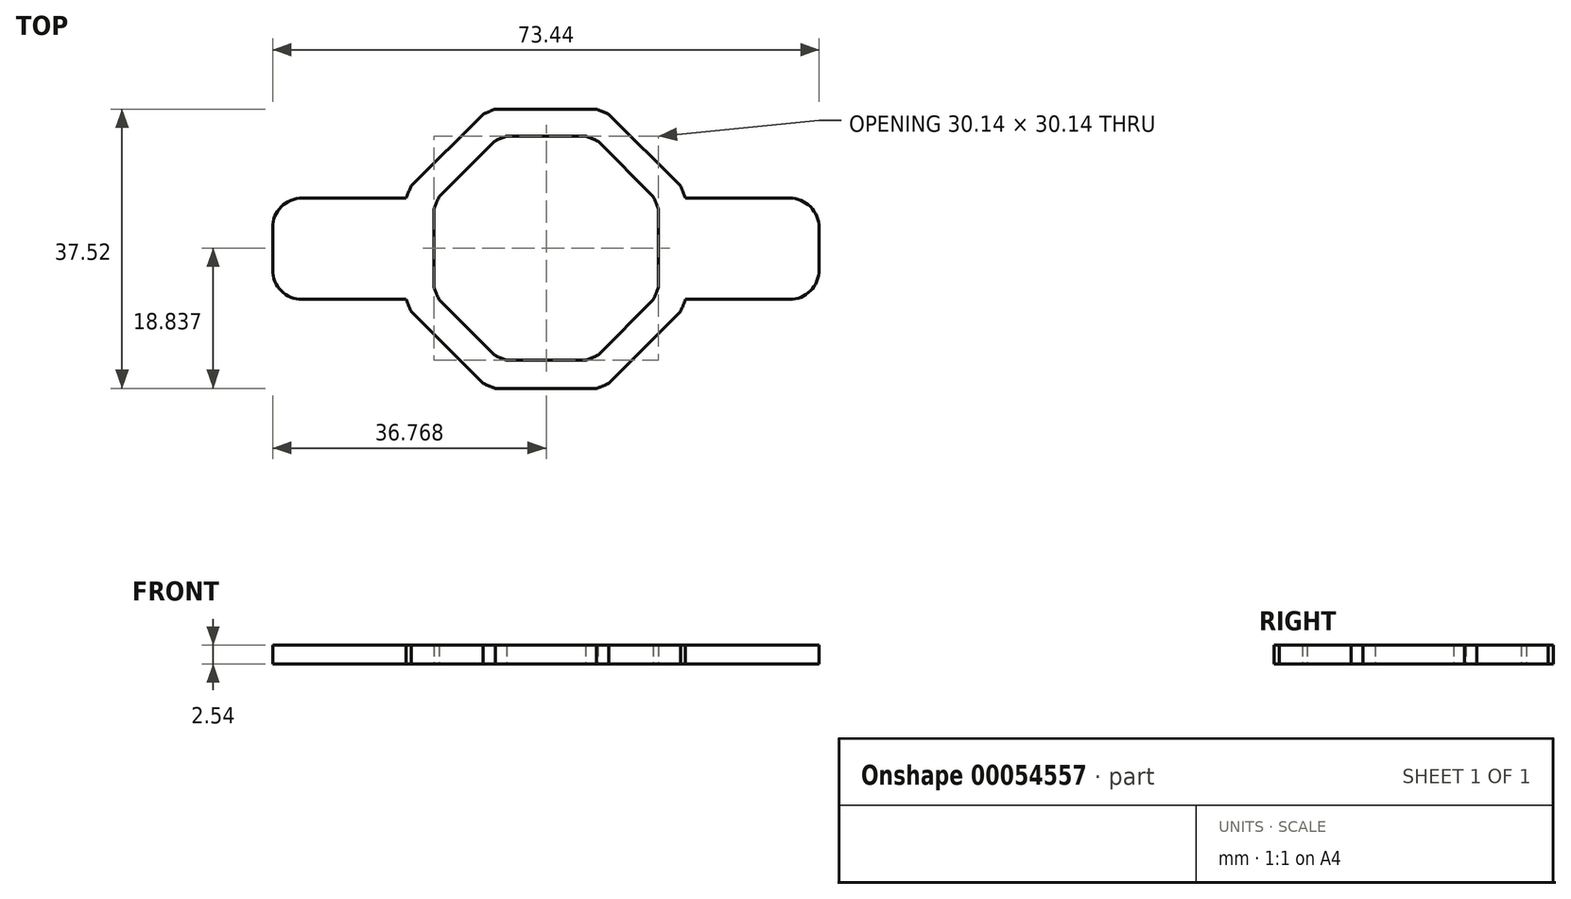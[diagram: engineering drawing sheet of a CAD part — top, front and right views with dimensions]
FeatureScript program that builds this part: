
annotation { "Feature Type Name" : "Feature", "Feature Type Description" : "" }
export const myFeature = defineFeature(function(context is Context, id is Id, definition is map)
    precondition{}
    {
        {
            var Q0;
            Q0=qCreatedBy(makeId("Top.planeOp"),FACE);
            var sketch = newSketch(context, id + "F0", { "sketchPlane" : qUnion([Q0])});
            skArc(sketch, "E0", {"start": v(-18.08, 8.45) * mm, "mid": v(-18.44, 7.64) * mm, "end": v(-18.76, 6.8) * mm});
            skLineSegment(sketch, "E1", {"start": v(-6.8, 18.76) * mm, "end": v(6.8, 18.76) * mm});
            skPoint(sketch, "E2.end.orphan", {"position": v(0, 18.76) * mm});
            skPoint(sketch, "E2.start.orphan", {"position": v(0, 19.96) * mm});
            skLineSegment(sketch, "E3.1.0", {"start": v(-18.08, 8.45) * mm, "end": v(-8.45, 18.08) * mm});
            skLineSegment(sketch, "E3.2.0", {"start": v(-18.76, -6.8) * mm, "end": v(-18.76, 6.8) * mm});
            skLineSegment(sketch, "E3.3.0", {"start": v(-8.45, -18.08) * mm, "end": v(-18.08, -8.45) * mm});
            skLineSegment(sketch, "E3.4.0", {"start": v(6.8, -18.76) * mm, "end": v(-6.8, -18.76) * mm});
            skLineSegment(sketch, "E3.5.0", {"start": v(18.08, -8.45) * mm, "end": v(8.45, -18.08) * mm});
            skLineSegment(sketch, "E3.6.0", {"start": v(18.76, 6.8) * mm, "end": v(18.76, -6.8) * mm});
            skLineSegment(sketch, "E3.7.0", {"start": v(8.45, 18.08) * mm, "end": v(18.08, 8.45) * mm});
            skArc(sketch, "E4.trimOffspring", {"start": v(-6.8, 18.76) * mm, "mid": v(-7.64, 18.44) * mm, "end": v(-8.45, 18.08) * mm});
            skArc(sketch, "E5.trimOffspring", {"start": v(8.45, 18.08) * mm, "mid": v(7.64, 18.44) * mm, "end": v(6.8, 18.76) * mm});
            skArc(sketch, "E6.trimOffspring", {"start": v(18.76, 6.8) * mm, "mid": v(18.44, 7.64) * mm, "end": v(18.08, 8.45) * mm});
            skArc(sketch, "E7.trimOffspring", {"start": v(18.08, -8.45) * mm, "mid": v(18.44, -7.64) * mm, "end": v(18.76, -6.8) * mm});
            skArc(sketch, "E8.trimOffspring", {"start": v(-8.45, -18.08) * mm, "mid": v(-7.64, -18.44) * mm, "end": v(-6.8, -18.76) * mm});
            skArc(sketch, "E9.trimOffspring", {"start": v(-18.76, -6.8) * mm, "mid": v(-18.44, -7.64) * mm, "end": v(-18.08, -8.45) * mm});
            skArc(sketch, "E10.trimOffspring", {"start": v(6.8, -18.76) * mm, "mid": v(7.64, -18.44) * mm, "end": v(8.45, -18.08) * mm});
            skLineSegment(sketch, "E11.6.0", {"start": v(15.12, 5.36) * mm, "end": v(15.12, -5.2) * mm});
            skLineSegment(sketch, "E11.4.0", {"start": v(5.33, -15) * mm, "end": v(-5.23, -15) * mm});
            skLineSegment(sketch, "E11.3.0", {"start": v(-6.87, -14.31) * mm, "end": v(-14.34, -6.84) * mm});
            skLineSegment(sketch, "E11.7.0", {"start": v(6.97, 14.46) * mm, "end": v(14.43, 7) * mm});
            skLineSegment(sketch, "E11.5.0", {"start": v(14.43, -6.84) * mm, "end": v(6.97, -14.31) * mm});
            skPoint(sketch, "E12.start.orphan", {"position": v(0.05, 16.04) * mm});
            skLineSegment(sketch, "E11.2.0", {"start": v(-15.02, -5.2) * mm, "end": v(-15.02, 5.36) * mm});
            skLineSegment(sketch, "E11.1.0", {"start": v(-14.34, 7) * mm, "end": v(-6.87, 14.46) * mm});
            skLineSegment(sketch, "E13", {"start": v(-5.23, 15.14) * mm, "end": v(5.33, 15.14) * mm});
            skPoint(sketch, "E12.end.orphan", {"position": v(0.05, 15.14) * mm});
            skPoint(sketch, "E11.center", {"position": v(0.05, 0.08) * mm});
            skArc(sketch, "E14.trimOffspring", {"start": v(5.33, -15) * mm, "mid": v(6.16, -14.67) * mm, "end": v(6.97, -14.31) * mm});
            skArc(sketch, "E15.trimOffspring", {"start": v(6.97, 14.46) * mm, "mid": v(6.16, 14.83) * mm, "end": v(5.33, 15.14) * mm});
            skArc(sketch, "E16.trimOffspring", {"start": v(-5.23, 15.14) * mm, "mid": v(-6.06, 14.83) * mm, "end": v(-6.87, 14.46) * mm});
            skArc(sketch, "E17", {"start": v(-14.34, 7) * mm, "mid": v(-14.7, 6.19) * mm, "end": v(-15.02, 5.36) * mm});
            skArc(sketch, "E18.trimOffspring", {"start": v(15.12, 5.36) * mm, "mid": v(14.8, 6.19) * mm, "end": v(14.43, 7) * mm});
            skArc(sketch, "E19.trimOffspring", {"start": v(-15.02, -5.2) * mm, "mid": v(-14.7, -6.03) * mm, "end": v(-14.34, -6.84) * mm});
            skArc(sketch, "E20.trimOffspring", {"start": v(-6.87, -14.31) * mm, "mid": v(-6.06, -14.67) * mm, "end": v(-5.23, -15) * mm});
            skArc(sketch, "E21.trimOffspring", {"start": v(14.43, -6.84) * mm, "mid": v(14.8, -6.03) * mm, "end": v(15.12, -5.2) * mm});
            skLineSegment(sketch, "E22.bottom", {"start": v(-18.76, 6.8) * mm, "end": v(-32.73, 6.8) * mm});
            skLineSegment(sketch, "E22.top", {"start": v(-18.76, -6.8) * mm, "end": v(-32.73, -6.8) * mm});
            skLineSegment(sketch, "E22.right", {"start": v(-36.72, 2.82) * mm, "end": v(-36.72, -2.82) * mm});
            skLineSegment(sketch, "E23.bottom", {"start": v(18.76, 6.8) * mm, "end": v(32.73, 6.8) * mm});
            skLineSegment(sketch, "E23.top", {"start": v(18.76, -6.8) * mm, "end": v(32.73, -6.8) * mm});
            skLineSegment(sketch, "E23.right", {"start": v(36.72, 2.82) * mm, "end": v(36.72, -2.82) * mm});
            skPoint(sketch, "E24.visualSharp", {"position": v(-36.72, 6.8) * mm});
            skArc(sketch, "E24.filletArc", {"start": v(-32.73, 6.8) * mm, "mid": v(-35.55, 5.64) * mm, "end": v(-36.72, 2.82) * mm});
            skPoint(sketch, "E25.visualSharp", {"position": v(-36.72, -6.8) * mm});
            skArc(sketch, "E25.filletArc", {"start": v(-36.72, -2.82) * mm, "mid": v(-35.55, -5.64) * mm, "end": v(-32.73, -6.8) * mm});
            skPoint(sketch, "E26.visualSharp", {"position": v(36.72, 6.8) * mm});
            skArc(sketch, "E26.filletArc", {"start": v(36.72, 2.82) * mm, "mid": v(35.55, 5.64) * mm, "end": v(32.73, 6.8) * mm});
            skPoint(sketch, "E27.visualSharp", {"position": v(36.72, -6.8) * mm});
            skArc(sketch, "E27.filletArc", {"start": v(32.73, -6.8) * mm, "mid": v(35.55, -5.64) * mm, "end": v(36.72, -2.82) * mm});
            skSolve(sketch);
        }
        {
            var Q0;
            Q0=makeQuery(id+"F0.imprint","IMPRINT",FACE,{"disambiguationData":[TD([[makeQuery(id+"F0.imprint","IMPRINT",EDGE,{"derivedFrom":sQuery(id+"F0.wireOp",EDGE,"E0")}),1.0]])]});
            extrude(context, id + "F1", {"entities" : qUnion([Q0]), "depth" : 2.54 * mm});
        }
        {
            var Q0;
            Q0=makeQuery(id+"F0.imprint","IMPRINT",FACE,{"disambiguationData":[TD([[makeQuery(id+"F0.imprint","IMPRINT",EDGE,{"derivedFrom":sQuery(id+"F0.wireOp",EDGE,"E3.2.0")}),1.0]])]});
            var Q1;
            Q1=makeQuery(id+"F0.imprint","IMPRINT",FACE,{"disambiguationData":[TD([[makeQuery(id+"F0.imprint","IMPRINT",EDGE,{"derivedFrom":sQuery(id+"F0.wireOp",EDGE,"E3.6.0")}),1.0]])]});
            extrude(context, id + "F2", {"entities" : qUnion([Q0, Q1]), "operationType" : NewBodyOperationType.ADD, "depth" : 2.54 * mm});
        }
    });
